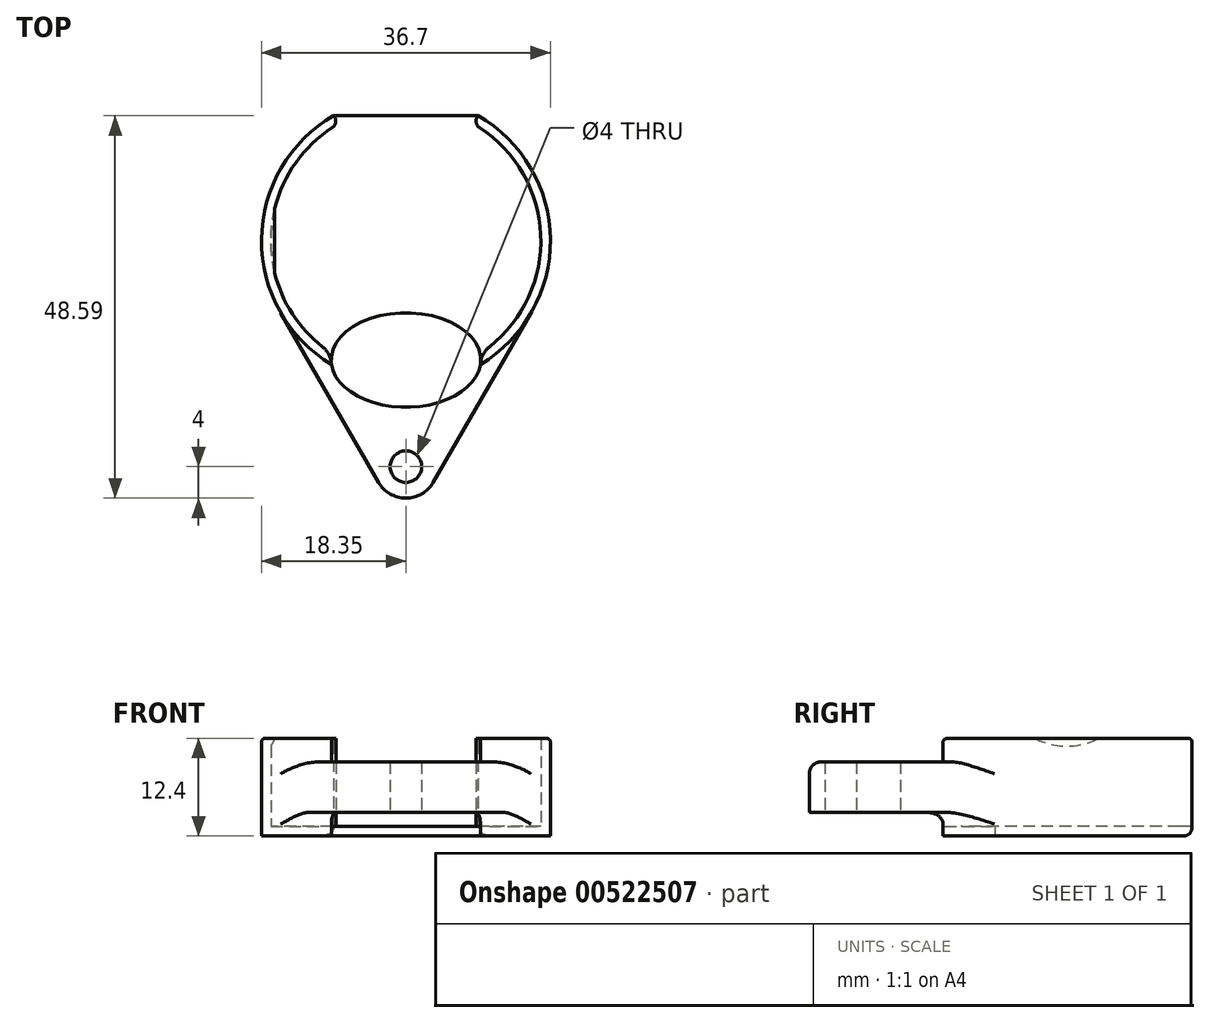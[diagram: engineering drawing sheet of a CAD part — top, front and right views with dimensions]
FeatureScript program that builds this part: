
annotation { "Feature Type Name" : "Feature", "Feature Type Description" : "" }
export const myFeature = defineFeature(function(context is Context, id is Id, definition is map)
    precondition{}
    {
        {
            var Q0;
            Q0=qCreatedBy(makeId("Top.planeOp"),FACE);
            var sketch = newSketch(context, id + "F0", { "sketchPlane" : qUnion([Q0])});
            skLineSegment(sketch, "E0", {"start": v(0, 0) * mm, "end": v(-9.18, 15.9) * mm, "construction": true});
            skLineSegment(sketch, "E1", {"start": v(-9.18, 15.9) * mm, "end": v(9.18, 15.9) * mm});
            skLineSegment(sketch, "E2", {"start": v(9.18, 15.9) * mm, "end": v(0, 0) * mm, "construction": true});
            skArc(sketch, "E3", {"start": v(-9.18, 15.9) * mm, "mid": v(0, -18.35) * mm, "end": v(9.18, 15.9) * mm});
            skArc(sketch, "E4", {"start": v(9.18, 15.9) * mm, "mid": v(0, 18.35) * mm, "end": v(-9.18, 15.9) * mm, "construction": true});
            skLineSegment(sketch, "E5", {"start": v(-15.9, -9.17) * mm, "end": v(-3.46, -30.7) * mm});
            skLineSegment(sketch, "E6", {"start": v(15.9, -9.17) * mm, "end": v(3.46, -30.7) * mm});
            skArc(sketch, "E7", {"start": v(-3.46, -30.7) * mm, "mid": v(0, -32.7) * mm, "end": v(3.46, -30.7) * mm});
            skCircle(sketch, "E8", {"center": v(0, -28.7) * mm, "radius": 2 * mm});
            skSolve(sketch);
        }
        {
            var Q0;
            {var subQ0=sQuery(id+"F0.wireOp",EDGE,"E1");Q0=makeQuery(id+"F0.imprint","IMPRINT",FACE,{"disambiguationData":[TD([[makeQuery(id+"F0.imprint","IMPRINT",EDGE,{"derivedFrom":subQ0}),-1.0]])]});}
            extrude(context, id + "F1", {"entities" : qUnion([Q0]), "depth" : 12.4 * mm, "offsetDistance" : 25 * mm});
        }
        {
            var Q0;
            {var subQ0=sQuery(id+"F0.wireOp",EDGE,"E1");Q0=makeQuery(id+"F0.imprint","IMPRINT",FACE,{"disambiguationData":[TD([[makeQuery(id+"F0.imprint","IMPRINT",EDGE,{"derivedFrom":subQ0}),-1.0]])]});}
            cPlane(context, id + "F2", {"entities" : qUnion([Q0]), "cplaneType" : CPlaneType.OFFSET, "offset" : 3 * mm, "width" : 150 * mm, "height" : 150 * mm});
        }
        {
            var Q0;
            Q0=makeQuery(id+"F1.opExtrude","CAP_FACE",FACE,{"disambiguationData":[OSD([sQuery(id+"F0.wireOp",EDGE,"E1"),sQuery(id+"F0.wireOp",EDGE,"E3")])],"isStart":false});
            cPlane(context, id + "F3", {"entities" : qUnion([Q0]), "cplaneType" : CPlaneType.OFFSET, "offset" : 3 * mm, "oppositeDirection" : true, "width" : 150 * mm, "height" : 150 * mm});
        }
        {
            var Q0;
            Q0=makeQuery(id+"F1.opExtrude","CAP_FACE",FACE,{"disambiguationData":[OSD([sQuery(id+"F0.wireOp",EDGE,"E1"),sQuery(id+"F0.wireOp",EDGE,"E3")])],"isStart":false});
            var Q1;
            Q1=makeQuery(id+"F1.opExtrude","SWEPT_FACE",FACE,{"disambiguationData":[OSD([sQuery(id+"F0.wireOp",EDGE,"E1")])]});
            shell(context, id + "F4", {"entities" : qUnion([Q0, Q1]), "thickness" : 1.2 * mm});
        }
        {
            var Q0;
            {var subQ1=sQuery(id+"F0.wireOp",EDGE,"E5");Q0=makeQuery(id+"F0.imprint","IMPRINT",FACE,{"disambiguationData":[TD([[makeQuery(id+"F0.imprint","IMPRINT",EDGE,{"derivedFrom":subQ1}),1.0]])]});}
            var Q1;
            Q1=qCreatedBy(id+"F3.planeOp",FACE);
            extrude(context, id + "F5", {"entities" : qUnion([Q0]), "operationType" : NewBodyOperationType.ADD, "endBound" : BoundingType.UP_TO_SURFACE, "depth" : 25 * mm, "endBoundEntityFace" : qUnion([Q1]), "offsetDistance" : 25 * mm});
        }
        {
            var Q0;
            {var subQ1=sQuery(id+"F0.wireOp",EDGE,"E5");Q0=makeQuery(id+"F0.imprint","IMPRINT",FACE,{"disambiguationData":[TD([[makeQuery(id+"F0.imprint","IMPRINT",EDGE,{"derivedFrom":subQ1}),1.0]])]});}
            var Q1;
            Q1=qCreatedBy(id+"F2.planeOp",FACE);
            extrude(context, id + "F6", {"entities" : qUnion([Q0]), "operationType" : NewBodyOperationType.REMOVE, "endBound" : BoundingType.UP_TO_SURFACE, "depth" : 25 * mm, "endBoundEntityFace" : qUnion([Q1]), "offsetDistance" : 25 * mm});
        }
        {
            var Q0;
            Q0=qCreatedBy(makeId("Front.planeOp"),FACE);
            var sketch = newSketch(context, id + "F7", { "sketchPlane" : qUnion([Q0])});
            skLineSegment(sketch, "E9", {"start": v(-17.15, 12.4) * mm, "end": v(-16.65, 12.4) * mm});
            skLineSegment(sketch, "E10", {"start": v(-16.65, 12.4) * mm, "end": v(-17.15, 11.4) * mm});
            skLineSegment(sketch, "E11", {"start": v(-17.15, 11.4) * mm, "end": v(-17.15, 12.4) * mm});
            skLineSegment(sketch, "E12.0", {"start": v(-17.15, 12.4) * mm, "end": v(17.15, 12.4) * mm});
            skSolve(sketch);
        }
        {
            var Q0;
            {var subQ0=sQuery(id+"F7.wireOp",EDGE,"E10");Q0=makeQuery(id+"F7.imprint","IMPRINT",FACE,{"disambiguationData":[TD([[makeQuery(id+"F7.imprint","IMPRINT",EDGE,{"derivedFrom":subQ0}),-1.0]])]});}
            var Q1;
            Q1=makeQuery(id+"F4.opShell","OFFSET_FACE",FACE,{"disambiguationData":[OSD([sQuery(id+"F0.wireOp",EDGE,"E3")])]});
            var Q2;
            Q2=makeQuery(id+"F4.opShell","OFFSET_FACE",FACE,{"disambiguationData":[OSD([sQuery(id+"F0.wireOp",EDGE,"E3")])]});
            extrude(context, id + "F8", {"entities" : qUnion([Q0]), "operationType" : NewBodyOperationType.ADD, "endBound" : BoundingType.UP_TO_SURFACE, "depth" : 25 * mm, "endBoundEntityFace" : qUnion([Q1]), "offsetDistance" : 25 * mm, "hasSecondDirection" : true, "secondDirectionBound" : SecondDirectionBoundingType.UP_TO_SURFACE, "secondDirectionOppositeDirection" : true, "secondDirectionDepth" : 25 * mm, "secondDirectionBoundEntityFace" : qUnion([Q2])});
        }
        {
            var Q0;
            {var subQ0=sQuery(id+"F0.wireOp",EDGE,"E3");var subQ1=sQuery(id+"F0.wireOp",EDGE,"E1");Q0=makeQuery(id+"F4.opShell","OFFSET_EDGE",EDGE,{"disambiguationData":[OSD([subQ1,subQ0]),TDD([makeQuery(id+"F1.opExtrude","SWEPT_EDGE",EDGE,{"disambiguationData":[OSD([subQ1,subQ0]),TDD([makeQuery(id+"F0.imprint","INTERSECT",VERTEX,{"disambiguationData":[OD(0.0)],"derivedFrom":[subQ1,subQ0]})])]})])]});}
            var Q1;
            {var subQ0=sQuery(id+"F0.wireOp",EDGE,"E3");var subQ1=sQuery(id+"F0.wireOp",EDGE,"E1");Q1=makeQuery(id+"F4.opShell","OFFSET_EDGE",EDGE,{"disambiguationData":[OSD([subQ1,subQ0]),TDD([makeQuery(id+"F1.opExtrude","SWEPT_EDGE",EDGE,{"disambiguationData":[OSD([subQ1,subQ0]),TDD([makeQuery(id+"F0.imprint","INTERSECT",VERTEX,{"disambiguationData":[OD(1.0)],"derivedFrom":[subQ1,subQ0]})])]})])]});}
            var Q2;
            Q2=makeQuery(id+"F1.opExtrude","CAP_EDGE",EDGE,{"disambiguationData":[OSD([sQuery(id+"F0.wireOp",EDGE,"E1")])],"isStart":true});
            fillet(context, id + "F9", {"entities" : qUnion([Q0, Q1, Q2]), "radius" : 1 * mm, "tangentPropagation" : true, "allowEdgeOverflow" : false});
        }
        {
            var Q0;
            {var subQ0=sQuery(id+"F0.wireOp",EDGE,"E3");var subQ4=sQuery(id+"F0.wireOp",EDGE,"E6");var subQ5=sQuery(id+"F0.wireOp",EDGE,"E5");var subQ8=makeQuery(id+"F1.opExtrude","CAP_EDGE",EDGE,{"disambiguationData":[OSD([subQ0])],"isStart":true});Q0=makeQuery(id+"F6.boolean.opBoolean","MERGE",EDGE,{"derivedFrom":[makeQuery(id+"F5.boolean.opBoolean","SPLIT",EDGE,{"disambiguationData":[TD([makeQuery(id+"F5.opExtrude","SWEPT_FACE",FACE,{"disambiguationData":[OSD([subQ5])]})])],"derivedFrom":subQ8}),makeQuery(id+"F5.boolean.opBoolean","SPLIT",EDGE,{"disambiguationData":[TD([makeQuery(id+"F5.opExtrude","SWEPT_FACE",FACE,{"disambiguationData":[OSD([subQ4])]})])],"derivedFrom":subQ8})],"fromTools":[makeQuery(id+"F6.opExtrude","CAP_EDGE",EDGE,{"disambiguationData":[OSD([subQ0])],"isStart":true})]});}
            var Q1;
            Q1=makeQuery(id+"F1.opExtrude","CAP_EDGE",EDGE,{"disambiguationData":[OSD([sQuery(id+"F0.wireOp",EDGE,"E3")])],"isStart":false});
            fillet(context, id + "F10", {"entities" : qUnion([Q0, Q1]), "radius" : .5 * mm, "allowEdgeOverflow" : false});
        }
        {
            var Q0;
            Q0=makeQuery(id+"F5.opExtrude","CAP_EDGE",EDGE,{"disambiguationData":[OSD([sQuery(id+"F0.wireOp",EDGE,"E3")])],"isStart":false});
            var Q1;
            Q1=makeQuery(id+"F5.opExtrude","CAP_EDGE",EDGE,{"disambiguationData":[OSD([sQuery(id+"F0.wireOp",EDGE,"E6")])],"isStart":false});
            var Q2;
            Q2=makeQuery(id+"F5.opExtrude","CAP_EDGE",EDGE,{"disambiguationData":[OSD([sQuery(id+"F0.wireOp",EDGE,"E7")])],"isStart":false});
            var Q3;
            Q3=makeQuery(id+"F5.opExtrude","CAP_EDGE",EDGE,{"disambiguationData":[OSD([sQuery(id+"F0.wireOp",EDGE,"E5")])],"isStart":false});
            var Q4;
            Q4=makeQuery(id+"F6.boolean.opBoolean","COPY",EDGE,{"derivedFrom":makeQuery(id+"F6.opExtrude","CAP_EDGE",EDGE,{"disambiguationData":[OSD([sQuery(id+"F0.wireOp",EDGE,"E3")])],"isStart":false})});
            var Q5;
            Q5=makeQuery(id+"F6.boolean.opBoolean","COPY",EDGE,{"derivedFrom":makeQuery(id+"F6.opExtrude","CAP_EDGE",EDGE,{"disambiguationData":[OSD([sQuery(id+"F0.wireOp",EDGE,"E6")])],"isStart":false})});
            var Q6;
            Q6=makeQuery(id+"F6.boolean.opBoolean","COPY",EDGE,{"derivedFrom":makeQuery(id+"F6.opExtrude","CAP_EDGE",EDGE,{"disambiguationData":[OSD([sQuery(id+"F0.wireOp",EDGE,"E7")])],"isStart":false})});
            var Q7;
            Q7=makeQuery(id+"F6.boolean.opBoolean","COPY",EDGE,{"derivedFrom":makeQuery(id+"F6.opExtrude","CAP_EDGE",EDGE,{"disambiguationData":[OSD([sQuery(id+"F0.wireOp",EDGE,"E5")])],"isStart":false})});
            fillet(context, id + "F11", {"entities" : qUnion([Q0, Q1, Q2, Q3, Q4, Q5, Q6, Q7]), "radius" : 1.5 * mm, "tangentPropagation" : true, "allowEdgeOverflow" : false});
        }
        {
            var Q0;
            Q0=qCreatedBy(makeId("Top.planeOp"),FACE);
            var sketch = newSketch(context, id + "F12", { "sketchPlane" : qUnion([Q0])});
            skArc(sketch, "E13.0", {"start": v(-9.36, 14.37) * mm, "mid": v(0, -17.15) * mm, "end": v(9.36, 14.37) * mm, "construction": true});
            skEllipse(sketch, "E14", {"center": v(0, -15.15) * mm, "majorRadius": 9.5 * mm, "minorRadius": 6 * mm, "majorAxis": v(1, 0)});
            skSolve(sketch);
        }
        {
            var Q0;
            Q0=makeQuery(id+"F12.imprint","IMPRINT",FACE,{"disambiguationData":[TD([[makeQuery(id+"F12.imprint","IMPRINT",EDGE,{"derivedFrom":sQuery(id+"F12.wireOp",EDGE,"E14")}),1.0]])]});
            var Q1;
            Q1=sQuery(id+"F12.wireOp",EDGE,"E14");
            extrude(context, id + "F13", {"entities" : qUnion([Q0]), "operationType" : NewBodyOperationType.REMOVE, "surfaceEntities" : qUnion([Q1]), "endBound" : BoundingType.THROUGH_ALL, "depth" : 25 * mm, "offsetDistance" : 25 * mm});
        }
        {
            var Q0;
            Q0=makeQuery(id+"F13.boolean.opBoolean","INTERSECT",EDGE,{"disambiguationData":[OD(0.0)],"derivedFrom":[makeQuery(id+"F4.opShell","OFFSET_FACE",FACE,{"disambiguationData":[OSD([sQuery(id+"F0.wireOp",EDGE,"E3")])]}),makeQuery(id+"F13.opExtrude","SWEPT_FACE",FACE,{"disambiguationData":[OSD([sQuery(id+"F12.wireOp",EDGE,"E14")])]})]});
            var Q1;
            Q1=makeQuery(id+"F13.boolean.opBoolean","INTERSECT",EDGE,{"disambiguationData":[OD(1.0)],"derivedFrom":[makeQuery(id+"F4.opShell","OFFSET_FACE",FACE,{"disambiguationData":[OSD([sQuery(id+"F0.wireOp",EDGE,"E3")])]}),makeQuery(id+"F13.opExtrude","SWEPT_FACE",FACE,{"disambiguationData":[OSD([sQuery(id+"F12.wireOp",EDGE,"E14")])]})]});
            fillet(context, id + "F14", {"entities" : qUnion([Q0, Q1]), "radius" : 3 * mm, "tangentPropagation" : true, "allowEdgeOverflow" : false});
        }
    });
